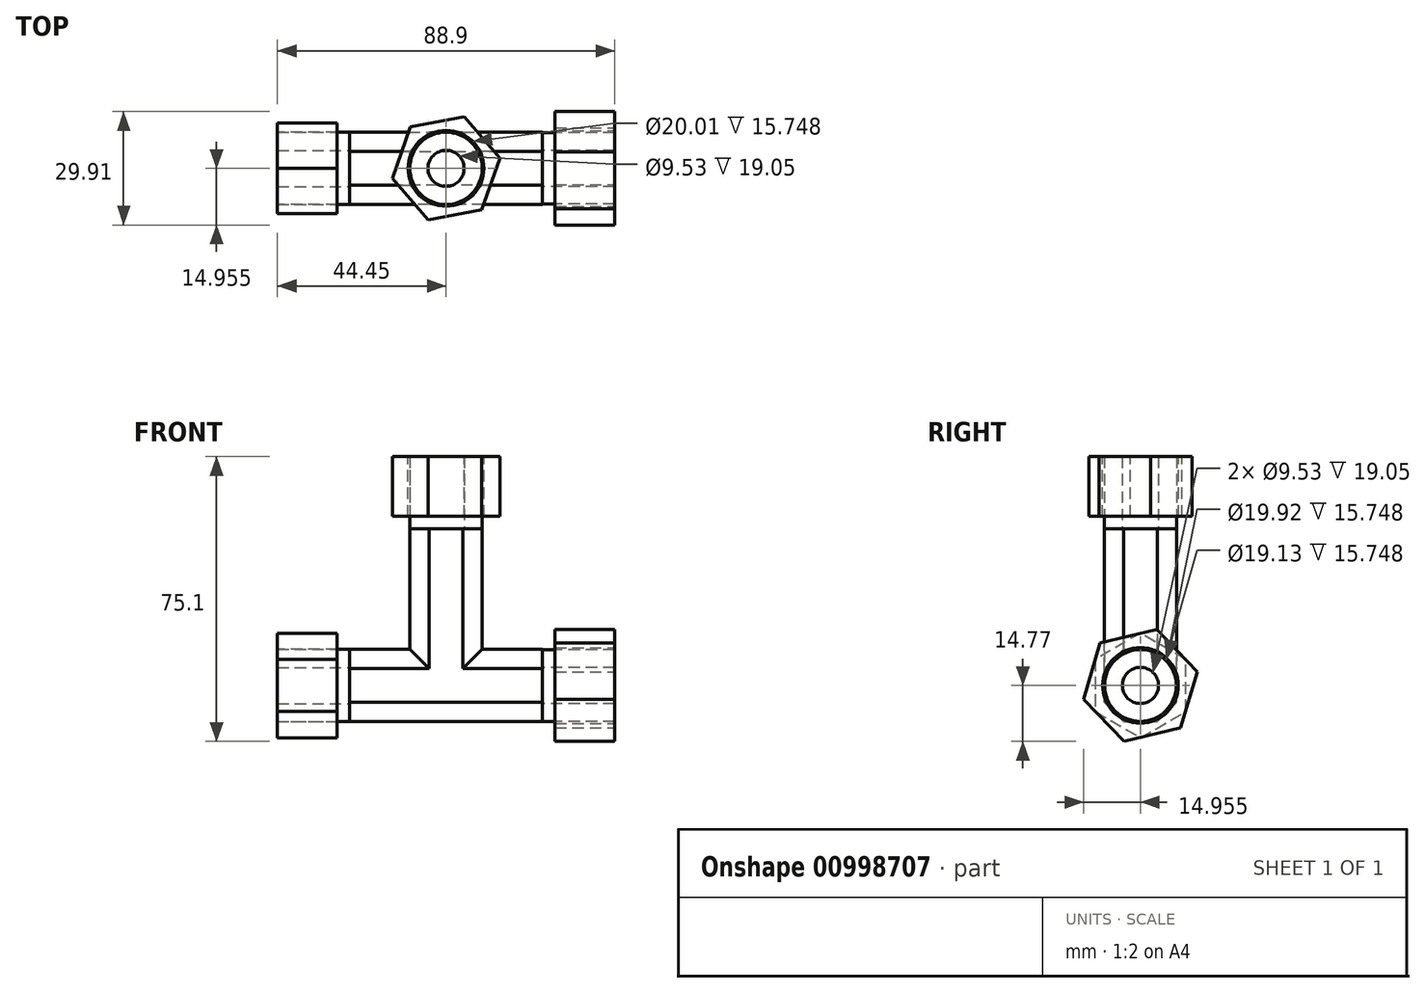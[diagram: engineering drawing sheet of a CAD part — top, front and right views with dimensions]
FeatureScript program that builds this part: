
annotation { "Feature Type Name" : "Feature", "Feature Type Description" : "" }
export const myFeature = defineFeature(function(context is Context, id is Id, definition is map)
    precondition{}
    {
        {
            var Q0;
            Q0=qCreatedBy(makeId("Front.planeOp"),FACE);
            var sketch = newSketch(context, id + "F0", { "sketchPlane" : qUnion([Q0])});
            skLineSegment(sketch, "E0.bottom", {"start": v(25.4, -9.52) * mm, "end": v(-25.4, -9.53) * mm});
            skLineSegment(sketch, "E0.top", {"start": v(25.4, 9.53) * mm, "end": v(9.53, 9.53) * mm});
            skLineSegment(sketch, "E0.left", {"start": v(25.4, -9.52) * mm, "end": v(25.4, 9.53) * mm});
            skLineSegment(sketch, "E0.right", {"start": v(-25.4, -9.53) * mm, "end": v(-25.4, 9.52) * mm});
            skPoint(sketch, "E0.middle", {"position": v(0, 0) * mm});
            skLineSegment(sketch, "E1.top", {"start": v(9.52, 41.28) * mm, "end": v(-9.53, 41.28) * mm});
            skLineSegment(sketch, "E1.left", {"start": v(9.53, 9.53) * mm, "end": v(9.52, 41.28) * mm});
            skLineSegment(sketch, "E1.right", {"start": v(-9.52, 9.53) * mm, "end": v(-9.53, 41.28) * mm});
            skPoint(sketch, "E1.middle", {"position": v(0, 25.4) * mm});
            skLineSegment(sketch, "E2.trimOffspring", {"start": v(-9.52, 9.52) * mm, "end": v(-25.4, 9.52) * mm});
            skSolve(sketch);
        }
        {
            var Q0;
            Q0 = qSketchRegion(id + "F0", true);
            extrude(context, id + "F1", {"entities" : qUnion([Q0]), "depth" : 19.05 * mm, "offsetDistance" : 25.4 * mm});
        }
        {
            var Q0;
            Q0=makeQuery(id+"F1.opExtrude","SWEPT_FACE",FACE,{"disambiguationData":[OSD([sQuery(id+"F0.wireOp",EDGE,"E0.left")])]});
            var sketch = newSketch(context, id + "F2", { "sketchPlane" : qUnion([Q0])});
            skCircle(sketch, "E3", {"center": v(-9.53, 0) * mm, "radius": 9.44 * mm});
            skPoint(sketch, "E3.centerSnap0", {"position": v(-9.53, 9.53) * mm});
            skCircle(sketch, "E4", {"center": v(-9.53, 0) * mm, "radius": 4.76 * mm});
            skSolve(sketch);
        }
        {
            var Q0;
            Q0 = qSketchRegion(id + "F2", true);
            extrude(context, id + "F3", {"entities" : qUnion([Q0]), "operationType" : NewBodyOperationType.ADD, "depth" : 19.05 * mm, "offsetDistance" : 25.4 * mm});
        }
        {
            var Q0;
            Q0=makeQuery(id+"F1.opExtrude","SWEPT_FACE",FACE,{"disambiguationData":[OSD([sQuery(id+"F0.wireOp",EDGE,"E0.right")])]});
            var sketch = newSketch(context, id + "F4", { "sketchPlane" : qUnion([Q0])});
            skCircle(sketch, "E5", {"center": v(9.53, 0) * mm, "radius": 9.52 * mm});
            skPoint(sketch, "E5.centerSnap0", {"position": v(9.53, 9.52) * mm});
            skCircle(sketch, "E6", {"center": v(9.53, 0) * mm, "radius": 4.76 * mm});
            skSolve(sketch);
        }
        {
            var Q0;
            Q0 = qSketchRegion(id + "F4", true);
            extrude(context, id + "F5", {"entities" : qUnion([Q0]), "operationType" : NewBodyOperationType.ADD, "depth" : 19.05 * mm, "offsetDistance" : 25.4 * mm});
        }
        {
            var Q0;
            Q0=makeQuery(id+"F1.opExtrude","SWEPT_FACE",FACE,{"disambiguationData":[OSD([sQuery(id+"F0.wireOp",EDGE,"E1.top")])]});
            var sketch = newSketch(context, id + "F6", { "sketchPlane" : qUnion([Q0])});
            skCircle(sketch, "E7", {"center": v(0, -9.53) * mm, "radius": 9.53 * mm});
            skPoint(sketch, "E7.centerSnap0", {"position": v(9.52, -9.53) * mm});
            skCircle(sketch, "E8", {"center": v(0, -9.53) * mm, "radius": 4.76 * mm});
            skSolve(sketch);
        }
        {
            var Q0;
            Q0 = qSketchRegion(id + "F6", true);
            extrude(context, id + "F7", {"entities" : qUnion([Q0]), "operationType" : NewBodyOperationType.ADD, "depth" : 19.05 * mm, "offsetDistance" : 25.4 * mm});
        }
        {
            var Q0;
            Q0=makeQuery(id+"F1.opExtrude","CAP_EDGE",EDGE,{"disambiguationData":[OSD([sQuery(id+"F0.wireOp",EDGE,"E1.right")])],"isStart":false});
            var Q1;
            Q1=makeQuery(id+"F1.opExtrude","CAP_EDGE",EDGE,{"disambiguationData":[OSD([sQuery(id+"F0.wireOp",EDGE,"E1.left")])],"isStart":false});
            var Q2;
            Q2=makeQuery(id+"F1.opExtrude","CAP_EDGE",EDGE,{"disambiguationData":[OSD([sQuery(id+"F0.wireOp",EDGE,"E0.top")])],"isStart":false});
            var Q3;
            Q3=makeQuery(id+"F1.opExtrude","CAP_EDGE",EDGE,{"disambiguationData":[OSD([sQuery(id+"F0.wireOp",EDGE,"E0.bottom")])],"isStart":true});
            var Q4;
            Q4=makeQuery(id+"F1.opExtrude","CAP_EDGE",EDGE,{"disambiguationData":[OSD([sQuery(id+"F0.wireOp",EDGE,"E0.bottom")])],"isStart":false});
            var Q5;
            Q5=makeQuery(id+"F1.opExtrude","CAP_EDGE",EDGE,{"disambiguationData":[OSD([sQuery(id+"F0.wireOp",EDGE,"E2.trimOffspring")])],"isStart":false});
            var Q6;
            Q6=makeQuery(id+"F1.opExtrude","CAP_EDGE",EDGE,{"disambiguationData":[OSD([sQuery(id+"F0.wireOp",EDGE,"E2.trimOffspring")])],"isStart":true});
            var Q7;
            Q7=makeQuery(id+"F1.opExtrude","CAP_EDGE",EDGE,{"disambiguationData":[OSD([sQuery(id+"F0.wireOp",EDGE,"E1.right")])],"isStart":true});
            var Q8;
            Q8=makeQuery(id+"F1.opExtrude","CAP_EDGE",EDGE,{"disambiguationData":[OSD([sQuery(id+"F0.wireOp",EDGE,"E1.left")])],"isStart":true});
            var Q9;
            Q9=makeQuery(id+"F1.opExtrude","CAP_EDGE",EDGE,{"disambiguationData":[OSD([sQuery(id+"F0.wireOp",EDGE,"E0.top")])],"isStart":true});
            chamfer(context, id + "F8", {"entities" : qUnion([Q0, Q1, Q2, Q3, Q4, Q5, Q6, Q7, Q8, Q9]), "width" : 5.08 * mm, "tangentPropagation" : true});
        }
        {
            var Q0;
            Q0=makeQuery(id+"F5.opExtrude","CAP_FACE",FACE,{"disambiguationData":[OSD([sQuery(id+"F4.wireOp",EDGE,"E5"),sQuery(id+"F4.wireOp",EDGE,"E6")])],"isStart":false});
            var sketch = newSketch(context, id + "F9", { "sketchPlane" : qUnion([Q0])});
            skCircle(sketch, "E9", {"center": v(9.53, 0) * mm, "radius": 9.56 * mm});
            skCircle(sketch, "E10.cCircle", {"center": v(9.53, 0) * mm, "radius": 11.94 * mm, "construction": true});
            skLineSegment(sketch, "E10.0", {"start": v(21.46, 6.9) * mm, "end": v(21.46, -6.9) * mm});
            skLineSegment(sketch, "E10.1", {"start": v(21.46, -6.9) * mm, "end": v(9.53, -13.78) * mm});
            skLineSegment(sketch, "E10.2", {"start": v(9.53, -13.78) * mm, "end": v(-2.41, -6.9) * mm});
            skLineSegment(sketch, "E10.3", {"start": v(-2.41, -6.9) * mm, "end": v(-2.41, 6.9) * mm});
            skLineSegment(sketch, "E10.4", {"start": v(-2.41, 6.9) * mm, "end": v(9.52, 13.78) * mm});
            skLineSegment(sketch, "E10.5", {"start": v(9.52, 13.78) * mm, "end": v(21.46, 6.9) * mm});
            skPoint(sketch, "E10.0.midPoint", {"position": v(21.46, 0) * mm});
            skSolve(sketch);
        }
        {
            var Q0;
            Q0 = qSketchRegion(id + "F9", true);
            extrude(context, id + "F10", {"entities" : qUnion([Q0]), "oppositeDirection" : true, "depth" : 15.75 * mm, "offsetDistance" : 25.4 * mm});
        }
        {
            var Q0;
            Q0=makeQuery(id+"F3.opExtrude","CAP_FACE",FACE,{"disambiguationData":[OSD([sQuery(id+"F2.wireOp",EDGE,"E3"),sQuery(id+"F2.wireOp",EDGE,"E4")])],"isStart":false});
            var sketch = newSketch(context, id + "F11", { "sketchPlane" : qUnion([Q0])});
            skCircle(sketch, "E11", {"center": v(-9.53, 0) * mm, "radius": 9.96 * mm});
            skCircle(sketch, "E12.cCircle", {"center": v(-9.53, 0) * mm, "radius": 13.33 * mm, "construction": true});
            skLineSegment(sketch, "E12.0", {"start": v(5.43, 3.63) * mm, "end": v(1.1, -11.14) * mm});
            skLineSegment(sketch, "E12.1", {"start": v(1.1, -11.14) * mm, "end": v(-13.86, -14.77) * mm});
            skLineSegment(sketch, "E12.2", {"start": v(-13.86, -14.77) * mm, "end": v(-24.48, -3.63) * mm});
            skLineSegment(sketch, "E12.3", {"start": v(-24.48, -3.63) * mm, "end": v(-20.14, 11.14) * mm});
            skLineSegment(sketch, "E12.4", {"start": v(-20.14, 11.14) * mm, "end": v(-5.19, 14.77) * mm});
            skLineSegment(sketch, "E12.5", {"start": v(-5.19, 14.77) * mm, "end": v(5.43, 3.63) * mm});
            skPoint(sketch, "E12.0.midPoint", {"position": v(3.26, -3.76) * mm});
            skSolve(sketch);
        }
        {
            var Q0;
            Q0 = qSketchRegion(id + "F11", true);
            extrude(context, id + "F12", {"entities" : qUnion([Q0]), "oppositeDirection" : true, "depth" : 15.75 * mm, "offsetDistance" : 25.4 * mm});
        }
        {
            var Q0;
            Q0=makeQuery(id+"F7.opExtrude","CAP_FACE",FACE,{"disambiguationData":[OSD([sQuery(id+"F6.wireOp",EDGE,"E7"),sQuery(id+"F6.wireOp",EDGE,"E8")])],"isStart":false});
            var sketch = newSketch(context, id + "F13", { "sketchPlane" : qUnion([Q0])});
            skCircle(sketch, "E13", {"center": v(0, -9.53) * mm, "radius": 10 * mm});
            skCircle(sketch, "E14.cCircle", {"center": v(0, -9.53) * mm, "radius": 12.47 * mm, "construction": true});
            skLineSegment(sketch, "E14.0", {"start": v(14.15, -6.85) * mm, "end": v(9.39, -20.44) * mm});
            skLineSegment(sketch, "E14.1", {"start": v(9.39, -20.44) * mm, "end": v(-4.76, -23.11) * mm});
            skLineSegment(sketch, "E14.2", {"start": v(-4.76, -23.11) * mm, "end": v(-14.15, -12.2) * mm});
            skLineSegment(sketch, "E14.3", {"start": v(-14.15, -12.2) * mm, "end": v(-9.39, 1.4) * mm});
            skLineSegment(sketch, "E14.4", {"start": v(-9.39, 1.4) * mm, "end": v(4.76, 4.06) * mm});
            skLineSegment(sketch, "E14.5", {"start": v(4.76, 4.06) * mm, "end": v(14.15, -6.85) * mm});
            skPoint(sketch, "E14.0.midPoint", {"position": v(11.77, -13.65) * mm});
            skSolve(sketch);
        }
        {
            var Q0;
            Q0 = qSketchRegion(id + "F13", true);
            extrude(context, id + "F14", {"entities" : qUnion([Q0]), "oppositeDirection" : true, "depth" : 15.75 * mm, "offsetDistance" : 25.4 * mm});
        }
    });
